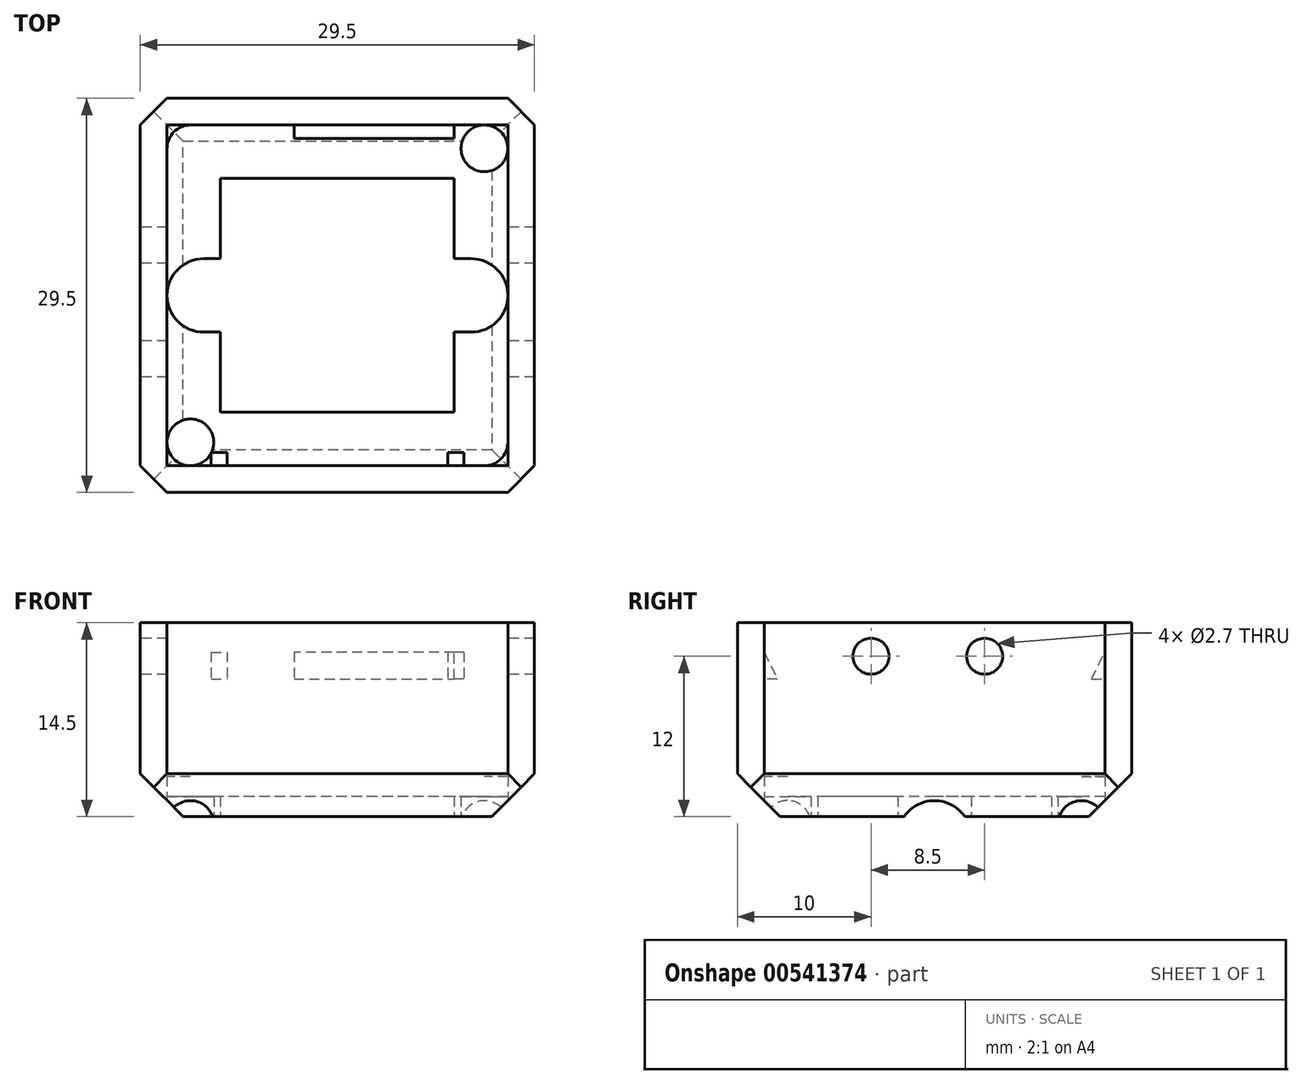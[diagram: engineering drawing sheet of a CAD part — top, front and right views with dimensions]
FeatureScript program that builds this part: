
annotation { "Feature Type Name" : "Feature", "Feature Type Description" : "" }
export const myFeature = defineFeature(function(context is Context, id is Id, definition is map)
    precondition{}
    {
        {
            var Q0;
            Q0=qCreatedBy(makeId("Top.planeOp"),FACE);
            var sketch = newSketch(context, id + "F0", { "sketchPlane" : qUnion([Q0])});
            skLineSegment(sketch, "E0.bottom", {"start": v(12.75, 12.75) * mm, "end": v(-12.75, 12.75) * mm});
            skLineSegment(sketch, "E0.top", {"start": v(12.75, -12.75) * mm, "end": v(-12.75, -12.75) * mm});
            skLineSegment(sketch, "E0.left", {"start": v(12.75, 12.75) * mm, "end": v(12.75, -12.75) * mm});
            skLineSegment(sketch, "E0.right", {"start": v(-12.75, 12.75) * mm, "end": v(-12.75, -12.75) * mm});
            skPoint(sketch, "E0.middle", {"position": v(0, 0) * mm});
            skLineSegment(sketch, "E1.bottom", {"start": v(14.75, 14.75) * mm, "end": v(-14.75, 14.75) * mm});
            skLineSegment(sketch, "E1.top", {"start": v(14.75, -14.75) * mm, "end": v(-14.75, -14.75) * mm});
            skLineSegment(sketch, "E1.left", {"start": v(14.75, 14.75) * mm, "end": v(14.75, -14.75) * mm});
            skLineSegment(sketch, "E1.right", {"start": v(-14.75, 14.75) * mm, "end": v(-14.75, -14.75) * mm});
            skLineSegment(sketch, "E2.bottom", {"start": v(8.75, 8.75) * mm, "end": v(-8.75, 8.75) * mm});
            skLineSegment(sketch, "E2.top", {"start": v(8.75, -8.75) * mm, "end": v(-8.75, -8.75) * mm});
            skLineSegment(sketch, "E2.right", {"start": v(-8.75, 8.75) * mm, "end": v(-8.75, 2.75) * mm});
            skArc(sketch, "E3", {"start": v(-10, 2.75) * mm, "mid": v(-12.75, 0) * mm, "end": v(-10, -2.75) * mm});
            skPoint(sketch, "E3.centerSnap0", {"position": v(-8.75, 0) * mm});
            skLineSegment(sketch, "E4", {"start": v(-10, 2.75) * mm, "end": v(-8.75, 2.75) * mm});
            skLineSegment(sketch, "E5.MirrorCS", {"start": v(-10, -2.75) * mm, "end": v(-8.75, -2.75) * mm});
            skLineSegment(sketch, "E6.trimOffspring", {"start": v(-8.75, -2.75) * mm, "end": v(-8.75, -8.75) * mm});
            skLineSegment(sketch, "E7.MirrorCS", {"start": v(10, 2.75) * mm, "end": v(8.75, 2.75) * mm});
            skArc(sketch, "E8.MirrorCS", {"start": v(10, 2.75) * mm, "mid": v(12.75, 0) * mm, "end": v(10, -2.75) * mm});
            skLineSegment(sketch, "E9.MirrorCS", {"start": v(10, -2.75) * mm, "end": v(8.75, -2.75) * mm});
            skLineSegment(sketch, "E10.MirrorCS", {"start": v(8.75, -2.75) * mm, "end": v(8.75, -8.75) * mm});
            skLineSegment(sketch, "E11.MirrorCS", {"start": v(8.75, 8.75) * mm, "end": v(8.75, 2.75) * mm});
            skCircle(sketch, "E12", {"center": v(-11, 11) * mm, "radius": 1.75 * mm});
            skCircle(sketch, "E13.MirrorC", {"center": v(11, 11) * mm, "radius": 1.75 * mm});
            skCircle(sketch, "E14.MirrorC", {"center": v(-11, -11) * mm, "radius": 1.75 * mm});
            skCircle(sketch, "E15.MirrorC", {"center": v(11, -11) * mm, "radius": 1.75 * mm});
            skSolve(sketch);
        }
        {
            var Q0;
            Q0=makeQuery(id+"F0.imprint","IMPRINT",FACE,{"disambiguationData":[TD([[makeQuery(id+"F0.imprint","IMPRINT",EDGE,{"derivedFrom":sQuery(id+"F0.wireOp",EDGE,"E2.bottom")}),-1.0]])]});
            var Q1;
            Q1=makeQuery(id+"F0.imprint","IMPRINT",FACE,{"disambiguationData":[TD([[makeQuery(id+"F0.imprint","IMPRINT",EDGE,{"derivedFrom":sQuery(id+"F0.wireOp",EDGE,"E2.top")}),1.0]])]});
            var Q2;
            {var subQ0=sQuery(id+"F0.wireOp",EDGE,"E0.right");var subQ1=sQuery(id+"F0.wireOp",EDGE,"E0.top");var subQ2=makeQuery(id+"F0.imprint","INTERSECT",VERTEX,{"derivedFrom":[subQ1,subQ0]});Q2=makeQuery(id+"F0.imprint","IMPRINT",FACE,{"disambiguationData":[TD([[makeQuery(id+"F0.imprint","IMPRINT",EDGE,{"disambiguationData":[TD([[subQ2,1.0]])],"derivedFrom":subQ1}),-1.0]])]});}
            var Q3;
            {var subQ0=sQuery(id+"F0.wireOp",EDGE,"E0.right");var subQ1=sQuery(id+"F0.wireOp",EDGE,"E0.bottom");var subQ2=makeQuery(id+"F0.imprint","INTERSECT",VERTEX,{"derivedFrom":[subQ1,subQ0]});Q3=makeQuery(id+"F0.imprint","IMPRINT",FACE,{"disambiguationData":[TD([[makeQuery(id+"F0.imprint","IMPRINT",EDGE,{"disambiguationData":[TD([[subQ2,1.0]])],"derivedFrom":subQ1}),1.0]])]});}
            var Q4;
            {var subQ0=sQuery(id+"F0.wireOp",EDGE,"E0.left");var subQ1=sQuery(id+"F0.wireOp",EDGE,"E0.bottom");var subQ2=makeQuery(id+"F0.imprint","INTERSECT",VERTEX,{"derivedFrom":[subQ1,subQ0]});Q4=makeQuery(id+"F0.imprint","IMPRINT",FACE,{"disambiguationData":[TD([[makeQuery(id+"F0.imprint","IMPRINT",EDGE,{"disambiguationData":[TD([[subQ2,-1.0]])],"derivedFrom":subQ1}),1.0]])]});}
            var Q5;
            {var subQ0=sQuery(id+"F0.wireOp",EDGE,"E0.left");var subQ1=sQuery(id+"F0.wireOp",EDGE,"E0.top");var subQ2=makeQuery(id+"F0.imprint","INTERSECT",VERTEX,{"derivedFrom":[subQ1,subQ0]});Q5=makeQuery(id+"F0.imprint","IMPRINT",FACE,{"disambiguationData":[TD([[makeQuery(id+"F0.imprint","IMPRINT",EDGE,{"disambiguationData":[TD([[subQ2,-1.0]])],"derivedFrom":subQ1}),-1.0]])]});}
            var Q6;
            {var subQ0=sQuery(id+"F0.wireOp",EDGE,"E15.MirrorC");var subQ1=makeQuery(id+"F0.imprint","INTERSECT",VERTEX,{"derivedFrom":[sQuery(id+"F0.wireOp",EDGE,"E0.top"),subQ0]});Q6=makeQuery(id+"F0.imprint","IMPRINT",FACE,{"disambiguationData":[TD([[makeQuery(id+"F0.imprint","IMPRINT",EDGE,{"disambiguationData":[TD([[subQ1,-1.0]])],"derivedFrom":subQ0}),1.0]])]});}
            var Q7;
            {var subQ0=sQuery(id+"F0.wireOp",EDGE,"E13.MirrorC");var subQ1=makeQuery(id+"F0.imprint","INTERSECT",VERTEX,{"derivedFrom":[sQuery(id+"F0.wireOp",EDGE,"E0.bottom"),subQ0]});Q7=makeQuery(id+"F0.imprint","IMPRINT",FACE,{"disambiguationData":[TD([[makeQuery(id+"F0.imprint","IMPRINT",EDGE,{"disambiguationData":[TD([[subQ1,-1.0]])],"derivedFrom":subQ0}),-1.0]])]});}
            var Q8;
            {var subQ0=sQuery(id+"F0.wireOp",EDGE,"E12");var subQ1=makeQuery(id+"F0.imprint","INTERSECT",VERTEX,{"derivedFrom":[sQuery(id+"F0.wireOp",EDGE,"E0.bottom"),subQ0]});Q8=makeQuery(id+"F0.imprint","IMPRINT",FACE,{"disambiguationData":[TD([[makeQuery(id+"F0.imprint","IMPRINT",EDGE,{"disambiguationData":[TD([[subQ1,-1.0]])],"derivedFrom":subQ0}),1.0]])]});}
            var Q9;
            {var subQ0=sQuery(id+"F0.wireOp",EDGE,"E14.MirrorC");var subQ1=makeQuery(id+"F0.imprint","INTERSECT",VERTEX,{"derivedFrom":[sQuery(id+"F0.wireOp",EDGE,"E0.top"),subQ0]});Q9=makeQuery(id+"F0.imprint","IMPRINT",FACE,{"disambiguationData":[TD([[makeQuery(id+"F0.imprint","IMPRINT",EDGE,{"disambiguationData":[TD([[subQ1,-1.0]])],"derivedFrom":subQ0}),-1.0]])]});}
            extrude(context, id + "F1", {"entities" : qUnion([Q0, Q1, Q2, Q3, Q4, Q5, Q6, Q7, Q8, Q9]), "depth" : 3 * mm, "offsetDistance" : 25 * mm});
        }
        {
            var Q0;
            Q0=makeQuery(id+"F0.imprint","IMPRINT",FACE,{"disambiguationData":[TD([[makeQuery(id+"F0.imprint","IMPRINT",EDGE,{"derivedFrom":sQuery(id+"F0.wireOp",EDGE,"E1.bottom")}),1.0]])]});
            extrude(context, id + "F2", {"entities" : qUnion([Q0]), "operationType" : NewBodyOperationType.ADD, "depth" : 14.5 * mm, "offsetDistance" : 25 * mm});
        }
        {
            var Q0;
            {var subQ0=sQuery(id+"F0.wireOp",EDGE,"E12");var subQ1=makeQuery(id+"F0.imprint","INTERSECT",VERTEX,{"derivedFrom":[sQuery(id+"F0.wireOp",EDGE,"E0.bottom"),subQ0]});Q0=makeQuery(id+"F0.imprint","IMPRINT",FACE,{"disambiguationData":[TD([[makeQuery(id+"F0.imprint","IMPRINT",EDGE,{"disambiguationData":[TD([[subQ1,-1.0]])],"derivedFrom":subQ0}),1.0]])]});}
            var Q1;
            {var subQ0=sQuery(id+"F0.wireOp",EDGE,"E13.MirrorC");var subQ1=makeQuery(id+"F0.imprint","INTERSECT",VERTEX,{"derivedFrom":[sQuery(id+"F0.wireOp",EDGE,"E0.bottom"),subQ0]});Q1=makeQuery(id+"F0.imprint","IMPRINT",FACE,{"disambiguationData":[TD([[makeQuery(id+"F0.imprint","IMPRINT",EDGE,{"disambiguationData":[TD([[subQ1,-1.0]])],"derivedFrom":subQ0}),-1.0]])]});}
            var Q2;
            {var subQ0=sQuery(id+"F0.wireOp",EDGE,"E14.MirrorC");var subQ1=makeQuery(id+"F0.imprint","INTERSECT",VERTEX,{"derivedFrom":[sQuery(id+"F0.wireOp",EDGE,"E0.top"),subQ0]});Q2=makeQuery(id+"F0.imprint","IMPRINT",FACE,{"disambiguationData":[TD([[makeQuery(id+"F0.imprint","IMPRINT",EDGE,{"disambiguationData":[TD([[subQ1,-1.0]])],"derivedFrom":subQ0}),-1.0]])]});}
            var Q3;
            {var subQ0=sQuery(id+"F0.wireOp",EDGE,"E15.MirrorC");var subQ1=makeQuery(id+"F0.imprint","INTERSECT",VERTEX,{"derivedFrom":[sQuery(id+"F0.wireOp",EDGE,"E0.top"),subQ0]});Q3=makeQuery(id+"F0.imprint","IMPRINT",FACE,{"disambiguationData":[TD([[makeQuery(id+"F0.imprint","IMPRINT",EDGE,{"disambiguationData":[TD([[subQ1,-1.0]])],"derivedFrom":subQ0}),1.0]])]});}
            extrude(context, id + "F3", {"entities" : qUnion([Q0, Q1, Q2, Q3]), "operationType" : NewBodyOperationType.REMOVE, "depth" : 3 * mm, "offsetDistance" : 25 * mm});
        }
        {
            var Q0;
            {var subQ0=sQuery(id+"F0.wireOp",EDGE,"E13.MirrorC");var subQ1=makeQuery(id+"F0.imprint","INTERSECT",VERTEX,{"derivedFrom":[sQuery(id+"F0.wireOp",EDGE,"E0.bottom"),subQ0]});Q0=makeQuery(id+"F0.imprint","IMPRINT",FACE,{"disambiguationData":[TD([[makeQuery(id+"F0.imprint","IMPRINT",EDGE,{"disambiguationData":[TD([[subQ1,-1.0]])],"derivedFrom":subQ0}),-1.0]])]});}
            var Q1;
            {var subQ0=sQuery(id+"F0.wireOp",EDGE,"E12");var subQ1=makeQuery(id+"F0.imprint","INTERSECT",VERTEX,{"derivedFrom":[sQuery(id+"F0.wireOp",EDGE,"E0.bottom"),subQ0]});Q1=makeQuery(id+"F0.imprint","IMPRINT",FACE,{"disambiguationData":[TD([[makeQuery(id+"F0.imprint","IMPRINT",EDGE,{"disambiguationData":[TD([[subQ1,-1.0]])],"derivedFrom":subQ0}),1.0]])]});}
            var Q2;
            {var subQ0=sQuery(id+"F0.wireOp",EDGE,"E14.MirrorC");var subQ1=makeQuery(id+"F0.imprint","INTERSECT",VERTEX,{"derivedFrom":[sQuery(id+"F0.wireOp",EDGE,"E0.top"),subQ0]});Q2=makeQuery(id+"F0.imprint","IMPRINT",FACE,{"disambiguationData":[TD([[makeQuery(id+"F0.imprint","IMPRINT",EDGE,{"disambiguationData":[TD([[subQ1,-1.0]])],"derivedFrom":subQ0}),-1.0]])]});}
            var Q3;
            {var subQ0=sQuery(id+"F0.wireOp",EDGE,"E15.MirrorC");var subQ1=makeQuery(id+"F0.imprint","INTERSECT",VERTEX,{"derivedFrom":[sQuery(id+"F0.wireOp",EDGE,"E0.top"),subQ0]});Q3=makeQuery(id+"F0.imprint","IMPRINT",FACE,{"disambiguationData":[TD([[makeQuery(id+"F0.imprint","IMPRINT",EDGE,{"disambiguationData":[TD([[subQ1,-1.0]])],"derivedFrom":subQ0}),1.0]])]});}
            extrude(context, id + "F4", {"entities" : qUnion([Q0, Q1, Q2, Q3]), "operationType" : NewBodyOperationType.ADD, "depth" : 1.5 * mm, "offsetDistance" : 25 * mm});
        }
        {
            var Q0;
            Q0=makeQuery(id+"F2.opExtrude","SWEPT_FACE",FACE,{"disambiguationData":[OSD([sQuery(id+"F0.wireOp",EDGE,"E1.right")])]});
            var sketch = newSketch(context, id + "F5", { "sketchPlane" : qUnion([Q0])});
            skCircle(sketch, "E16", {"center": v(-3.75, 12) * mm, "radius": 1.35 * mm});
            skCircle(sketch, "E17", {"center": v(4.75, 12) * mm, "radius": 1.35 * mm});
            skSolve(sketch);
        }
        {
            var Q0;
            Q0=makeQuery(id+"F2.opExtrude","SWEPT_FACE",FACE,{"disambiguationData":[OSD([sQuery(id+"F0.wireOp",EDGE,"E0.bottom")])]});
            var sketch = newSketch(context, id + "F6", { "sketchPlane" : qUnion([Q0])});
            skLineSegment(sketch, "E18", {"start": v(-3.25, 10.3) * mm, "end": v(8.75, 10.3) * mm});
            skLineSegment(sketch, "E19", {"start": v(8.75, 10.3) * mm, "end": v(8.75, 12.3) * mm});
            skLineSegment(sketch, "E20", {"start": v(8.75, 12.3) * mm, "end": v(-3.25, 12.3) * mm});
            skLineSegment(sketch, "E21", {"start": v(-3.25, 12.3) * mm, "end": v(-3.25, 10.3) * mm});
            skSolve(sketch);
        }
        {
            var Q0;
            Q0=makeQuery(id+"F6.imprint","IMPRINT",FACE,{"disambiguationData":[TD([[makeQuery(id+"F6.imprint","IMPRINT",EDGE,{"derivedFrom":sQuery(id+"F6.wireOp",EDGE,"E18")}),1.0]])]});
            extrude(context, id + "F7", {"entities" : qUnion([Q0]), "operationType" : NewBodyOperationType.ADD, "depth" : 1 * mm, "offsetDistance" : 25 * mm});
        }
        {
            var Q0;
            Q0=makeQuery(id+"F7.opExtrude","CAP_EDGE",EDGE,{"disambiguationData":[OSD([sQuery(id+"F6.wireOp",EDGE,"E20")])],"isStart":false});
            chamfer(context, id + "F8", {"entities" : qUnion([Q0]), "chamferType" : ChamferType.TWO_OFFSETS, "width1" : 1 * mm, "oppositeDirection" : true, "width2" : 2 * mm, "tangentPropagation" : true});
        }
        {
            var Q0;
            Q0=makeQuery(id+"F2.opExtrude","SWEPT_FACE",FACE,{"disambiguationData":[OSD([sQuery(id+"F0.wireOp",EDGE,"E0.top")])]});
            var sketch = newSketch(context, id + "F9", { "sketchPlane" : qUnion([Q0])});
            skLineSegment(sketch, "E22.bottom", {"start": v(-9.45, 12.3) * mm, "end": v(-8.25, 12.3) * mm});
            skLineSegment(sketch, "E22.top", {"start": v(-9.45, 10.3) * mm, "end": v(-8.25, 10.3) * mm});
            skLineSegment(sketch, "E22.left", {"start": v(-9.45, 12.3) * mm, "end": v(-9.45, 10.3) * mm});
            skLineSegment(sketch, "E22.right", {"start": v(-8.25, 12.3) * mm, "end": v(-8.25, 10.3) * mm});
            skLineSegment(sketch, "E23.MirrorCS", {"start": v(9.45, 12.3) * mm, "end": v(9.45, 10.3) * mm});
            skLineSegment(sketch, "E24.MirrorCS", {"start": v(9.45, 12.3) * mm, "end": v(8.25, 12.3) * mm});
            skLineSegment(sketch, "E25.MirrorCS", {"start": v(8.25, 12.3) * mm, "end": v(8.25, 10.3) * mm});
            skLineSegment(sketch, "E26.MirrorCS", {"start": v(9.45, 10.3) * mm, "end": v(8.25, 10.3) * mm});
            skSolve(sketch);
        }
        {
            var Q0;
            Q0=makeQuery(id+"F9.imprint","IMPRINT",FACE,{"disambiguationData":[TD([[makeQuery(id+"F9.imprint","IMPRINT",EDGE,{"derivedFrom":sQuery(id+"F9.wireOp",EDGE,"E22.bottom")}),-1.0]])]});
            var Q1;
            Q1=makeQuery(id+"F9.imprint","IMPRINT",FACE,{"disambiguationData":[TD([[makeQuery(id+"F9.imprint","IMPRINT",EDGE,{"derivedFrom":sQuery(id+"F9.wireOp",EDGE,"E23.MirrorCS")}),-1.0]])]});
            extrude(context, id + "F10", {"entities" : qUnion([Q0, Q1]), "operationType" : NewBodyOperationType.ADD, "depth" : 1 * mm, "offsetDistance" : 25 * mm});
        }
        {
            var Q0;
            Q0=makeQuery(id+"F10.opExtrude","CAP_EDGE",EDGE,{"disambiguationData":[OSD([sQuery(id+"F9.wireOp",EDGE,"E22.bottom")])],"isStart":false});
            chamfer(context, id + "F11", {"entities" : qUnion([Q0]), "chamferType" : ChamferType.TWO_OFFSETS, "width1" : 1 * mm, "oppositeDirection" : false, "width2" : 2 * mm, "tangentPropagation" : true});
        }
        {
            var Q0;
            Q0=makeQuery(id+"F10.opExtrude","CAP_EDGE",EDGE,{"disambiguationData":[OSD([sQuery(id+"F9.wireOp",EDGE,"E24.MirrorCS")])],"isStart":false});
            chamfer(context, id + "F12", {"entities" : qUnion([Q0]), "chamferType" : ChamferType.TWO_OFFSETS, "width1" : 1 * mm, "oppositeDirection" : true, "width2" : 2 * mm, "tangentPropagation" : true});
        }
        {
            var Q0;
            Q0=makeQuery(id+"F2.opExtrude","CAP_EDGE",EDGE,{"disambiguationData":[OSD([sQuery(id+"F0.wireOp",EDGE,"E1.bottom")])],"isStart":true});
            var Q1;
            Q1=makeQuery(id+"F2.opExtrude","CAP_EDGE",EDGE,{"disambiguationData":[OSD([sQuery(id+"F0.wireOp",EDGE,"E1.right")])],"isStart":true});
            var Q2;
            Q2=makeQuery(id+"F2.opExtrude","CAP_EDGE",EDGE,{"disambiguationData":[OSD([sQuery(id+"F0.wireOp",EDGE,"E1.top")])],"isStart":true});
            var Q3;
            Q3=makeQuery(id+"F2.opExtrude","CAP_EDGE",EDGE,{"disambiguationData":[OSD([sQuery(id+"F0.wireOp",EDGE,"E1.left")])],"isStart":true});
            chamfer(context, id + "F13", {"entities" : qUnion([Q0, Q1, Q2, Q3]), "width" : 3.2 * mm, "tangentPropagation" : true});
        }
        {
            var Q0;
            Q0=makeQuery(id+"F5.imprint","IMPRINT",FACE,{"disambiguationData":[TD([[makeQuery(id+"F5.imprint","IMPRINT",EDGE,{"derivedFrom":sQuery(id+"F5.wireOp",EDGE,"E17")}),1.0]])]});
            var Q1;
            Q1=makeQuery(id+"F5.imprint","IMPRINT",FACE,{"disambiguationData":[TD([[makeQuery(id+"F5.imprint","IMPRINT",EDGE,{"derivedFrom":sQuery(id+"F5.wireOp",EDGE,"E16")}),1.0]])]});
            extrude(context, id + "F14", {"entities" : qUnion([Q0, Q1]), "operationType" : NewBodyOperationType.REMOVE, "oppositeDirection" : true, "depth" : 30 * mm, "offsetDistance" : 25 * mm});
        }
        {
            var Q0;
            Q0=makeQuery(id+"F2.opExtrude","SWEPT_EDGE",EDGE,{"disambiguationData":[OSD([sQuery(id+"F0.wireOp",EDGE,"E1.bottom"),sQuery(id+"F0.wireOp",EDGE,"E1.left")])]});
            var Q1;
            Q1=makeQuery(id+"F2.opExtrude","SWEPT_EDGE",EDGE,{"disambiguationData":[OSD([sQuery(id+"F0.wireOp",EDGE,"E1.bottom"),sQuery(id+"F0.wireOp",EDGE,"E1.right")])]});
            var Q2;
            Q2=makeQuery(id+"F2.opExtrude","SWEPT_EDGE",EDGE,{"disambiguationData":[OSD([sQuery(id+"F0.wireOp",EDGE,"E1.top"),sQuery(id+"F0.wireOp",EDGE,"E1.left")])]});
            var Q3;
            Q3=makeQuery(id+"F2.opExtrude","SWEPT_EDGE",EDGE,{"disambiguationData":[OSD([sQuery(id+"F0.wireOp",EDGE,"E1.top"),sQuery(id+"F0.wireOp",EDGE,"E1.right")])]});
            chamfer(context, id + "F15", {"entities" : qUnion([Q0, Q1, Q2, Q3]), "width" : 2 * mm, "tangentPropagation" : true});
        }
    });
